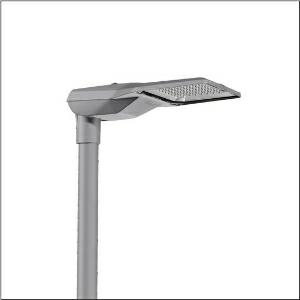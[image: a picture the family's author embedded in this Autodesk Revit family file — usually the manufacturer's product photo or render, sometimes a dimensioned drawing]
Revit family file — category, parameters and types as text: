
# Revit family: streetlight_sl_21_iq_midi___p0_8ab_5xe3r31v08mb_2caf
name_source: partatom
category: Lighting Fixtures
units: mm (PartAtom-declared; Revit-internal decimal feet)

## family parameters
Cut with Voids When Loaded = No
Host = Face
Light Source = No
Part Type = Normal
Room Calculation Point = No
Round Connector Dimension = Use Diameter
Shared = No

## types (1)
- --- (1 x LED, 15920 lm, 129.3 W, 3000K)
    Apparent Load = 129 VA
    CIE Flux Codes = 36 71 98 100 100
    Color Rendering = 70
    Color Temperature = 3000K
    Default Elevation = 1800 mm
    Description = Streetlight SL 21 iQ midi, mast luminaire, primary light control with lens, of PMMA, primary optical cover: cover, of toughened safety glass, transparent, light distribution: P0.8aB, light emission: direct distribution, primary light characteristic: asymmetric, installation type: post-top, side-entry, LED, High Power LED, rated luminous flux: 15.920lm, luminous efficacy: 123lm/W, light colour: 730, colour temperature: 3000K, control gear: iQ-Street Remote, D4i with power reduction, control: pre-setting: logarithmic dimming characteristic, Street-Remote, Auto-Match, Temp-Guard, Lumen-Switch, Night-Set, Smart-Wire, Light-Fading, Desk-Remote (wireless, voltage-free reading and setting of iQ features in the workshop via application-optimized NFC function/RFID function), optimised constant luminous flux control (CLO 2.0), mains connection: 230..240V, AC, 50/60Hz, start of lifetime: 129W, end of service life: 142W, reduction: 56W, luminaire housing, of diecast aluminium, powder-coated, Siteco® metallic grey (DB 702S), corrosivity category C5 mid according to DIN EN ISO 12944, please order mast flange separately, inclination adjustable: 0°, 5°, 10°, 15°, sealing non-destructively replaceable, multi-level sealing system, length: 644mm, width: 335mm, height: 110mm, mast flange for spigot size: 42mm (side-entry): 5XC10008XM4, 60/48mm (side-entry/post-top): 5XC10108XM2, 76/60mm (side-entry/post-top): 5XC10108XM1, mounting height: 4..8m, Smart Interface above, protection rating (complete): IP66, insulation class (complete): insulation class II (safety insulation), certification: CE, ENEC, ENEC+, VDE, impact resistance: IK10, permissible operating ambient temperature for outdoor applications: -40..+50°C, standard-compliant lighting for roads and squares, packaging unit: 1 piece

Light Distribution: P0.8aB
    Height = 111 mm
    Lamp = 1 x LED
    Lamp Light Flux = 15920 lm
    Lamp Power = 129.3 W
    Lamp count = 1
    Length = 644 mm
    Luminous efficacy = 123 lm/W
    Manufacturer = Siteco
    ModVariant = No
    Model = 5XE3R31V08MB
    Number of Poles = 1
    OnlyDefault = Yes
    Power Factor = 1
    Product Name = Streetlight SL 21 iQ midi | P0.8aB
    Product group = mast luminaire | pylon top
    ProductGroupID = 6100
    Protection Class = Protection class II
    Protection Degree = IP 66
    RLX_Detail_Level = 1
    RLX_Emergency_Light_Flux = 0 lm
    RLX_Emergency_Type = 0
    RLX_Emergency_Type_DB = No
    RlxData = <blob elided: 26773 chars, md5=e671bc79>
    Socket = socket
    Standby Power = 0 W
    System Light Flux = 15919 lm
    System Power = 129 W
    Type Comments = factory setting: luminous flux: 100 % | dim-lin: 254 | 672 mA
    Type Image = l_1004302.jpg
    URL = http://relux.com
    VarID = @adj_075234
    Voltage = 0 V
    Weight = 0.00 kg
    Width = 336 mm

## geometry (parser evidence)
native form markers: Blend x4, Sweep x10
no freeform markers — native parametric forms only
